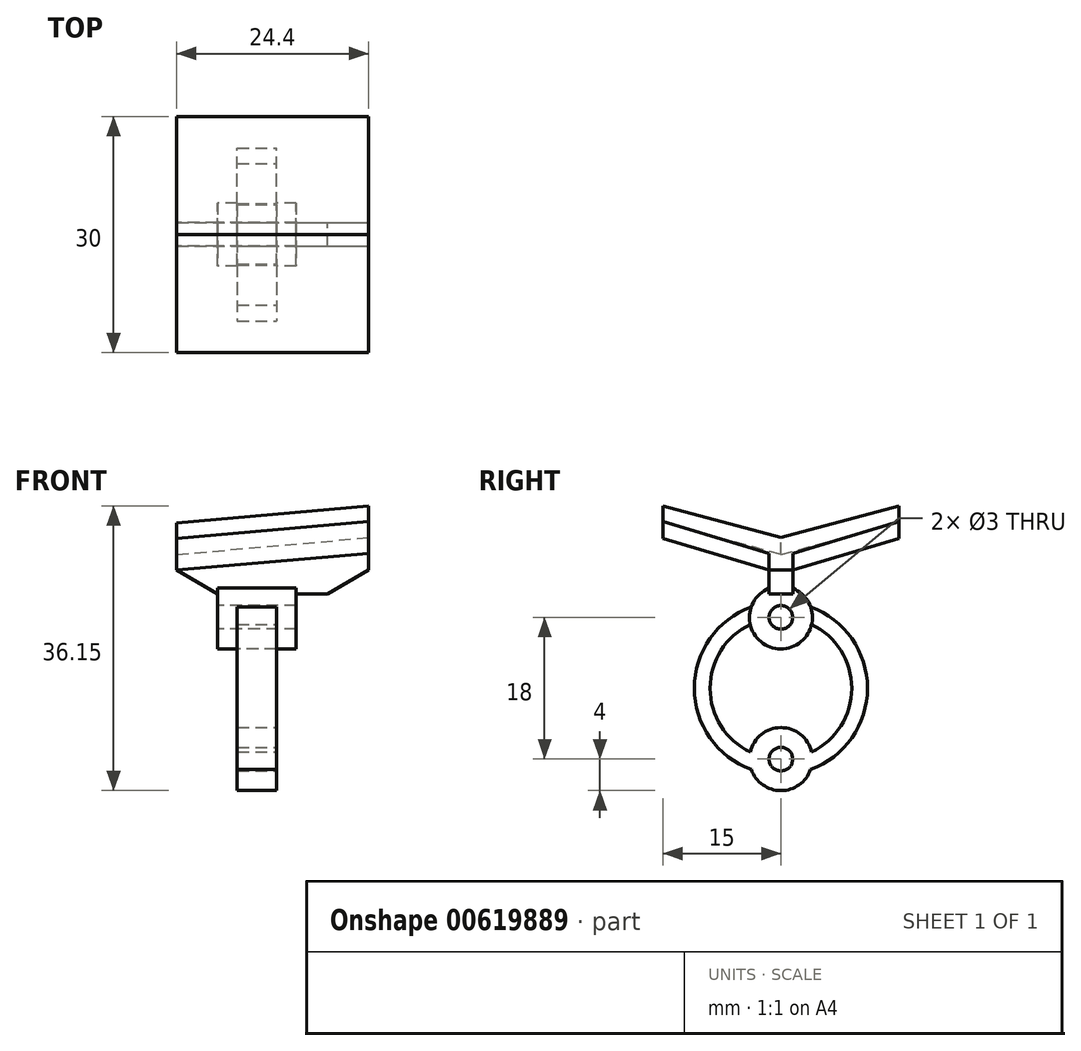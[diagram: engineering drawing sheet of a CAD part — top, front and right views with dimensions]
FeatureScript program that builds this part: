
annotation { "Feature Type Name" : "Feature", "Feature Type Description" : "" }
export const myFeature = defineFeature(function(context is Context, id is Id, definition is map)
    precondition{}
    {
        {
            var Q0;
            Q0=qCreatedBy(makeId("Right.planeOp"),FACE);
            var sketch = newSketch(context, id + "F0", { "sketchPlane" : qUnion([Q0])});
            skCircle(sketch, "E0", {"center": v(0, 0) * mm, "radius": 1.5 * mm});
            skCircle(sketch, "E1", {"center": v(0, 0) * mm, "radius": 4 * mm});
            skSolve(sketch);
        }
        {
            var Q0;
            Q0=makeQuery(id+"F0.imprint","IMPRINT",FACE,{"disambiguationData":[TD([[makeQuery(id+"F0.imprint","IMPRINT",EDGE,{"derivedFrom":sQuery(id+"F0.wireOp",EDGE,"E0")}),-1.0]])]});
            var Q1;
            Q1=qConstructionFilter(qBodyType(qCreatedBy(id+"F0",EDGE),BodyType.WIRE),ConstructionObject.NO);
            extrude(context, id + "F1", {"entities" : qUnion([Q0]), "surfaceEntities" : qUnion([Q1]), "depth" : 10 * mm, "offsetDistance" : 25 * mm});
        }
        {
            var Q0;
            Q0=qCreatedBy(makeId("Front.planeOp"),FACE);
            var sketch = newSketch(context, id + "F2", { "sketchPlane" : qUnion([Q0])});
            skLineSegment(sketch, "E2", {"start": v(0, 3) * mm, "end": v(14, 3) * mm});
            skLineSegment(sketch, "E3", {"start": v(0, 3) * mm, "end": v(-5.2, 6) * mm});
            skLineSegment(sketch, "E4", {"start": v(14, 3) * mm, "end": v(19.2, 6) * mm});
            skLineSegment(sketch, "E5", {"start": v(-5.2, 6) * mm, "end": v(-5.2, 8) * mm});
            skLineSegment(sketch, "E6", {"start": v(-5.2, 8) * mm, "end": v(19.2, 10.13) * mm});
            skLineSegment(sketch, "E7", {"start": v(19.2, 10.13) * mm, "end": v(19.2, 6) * mm});
            skSolve(sketch);
        }
        {
            var Q0;
            Q0=qSketchRegion(id+"F2",true);
            extrude(context, id + "F3", {"entities" : qUnion([Q0]), "operationType" : NewBodyOperationType.ADD, "endBound" : BoundingType.SYMMETRIC, "depth" : 3 * mm, "offsetDistance" : 25 * mm});
        }
        {
            var Q0;
            Q0=makeQuery(id+"F3.opExtrude","SWEPT_FACE",FACE,{"disambiguationData":[OSD([sQuery(id+"F2.wireOp",EDGE,"E5")])]});
            var sketch = newSketch(context, id + "F4", { "sketchPlane" : qUnion([Q0])});
            skLineSegment(sketch, "E8", {"start": v(0, 8) * mm, "end": v(0, 13) * mm, "construction": true});
            skPoint(sketch, "E8.endSnap0", {"position": v(0, 8) * mm});
            skLineSegment(sketch, "E9", {"start": v(0, 8) * mm, "end": v(15, 12.02) * mm});
            skLineSegment(sketch, "E10", {"start": v(0, 8) * mm, "end": v(10.53, 8) * mm, "construction": true});
            skLineSegment(sketch, "E11", {"start": v(15, 12.02) * mm, "end": v(15, 10.02) * mm});
            skLineSegment(sketch, "E12", {"start": v(15, 10.02) * mm, "end": v(1.5, 6) * mm});
            skLineSegment(sketch, "E13", {"start": v(1.5, 6) * mm, "end": v(0, 8) * mm});
            skLineSegment(sketch, "E14.MirrorCS", {"start": v(0, 8) * mm, "end": v(-15, 12.02) * mm});
            skLineSegment(sketch, "E15.MirrorCS", {"start": v(-1.5, 6) * mm, "end": v(0, 8) * mm});
            skLineSegment(sketch, "E16.MirrorCS", {"start": v(-15, 10.02) * mm, "end": v(-1.5, 6) * mm});
            skLineSegment(sketch, "E17.MirrorCS", {"start": v(-15, 12.02) * mm, "end": v(-15, 10.02) * mm});
            skSolve(sketch);
        }
        {
            var Q0;
            Q0=makeQuery(id+"F3.opExtrude","SWEPT_FACE",FACE,{"disambiguationData":[OSD([sQuery(id+"F2.wireOp",EDGE,"E6")])]});
            var sketch = newSketch(context, id + "F5", { "sketchPlane" : qUnion([Q0])});
            skLineSegment(sketch, "E18", {"start": v(-4.48, 0) * mm, "end": v(20, 0) * mm});
            skSolve(sketch);
        }
        {
            var Q0;
            Q0 = qSketchRegion(id + "F4", true);
            var Q1;
            Q1 = qConstructionFilter(qBodyType(qCreatedBy(id + "F5" ,EDGE), BodyType.WIRE), ConstructionObject.NO);
            sweep(context, id + "F6", {"operationType" : NewBodyOperationType.ADD, "profiles" : qUnion([Q0]), "path" : qUnion([Q1])});
        }
        {
            var Q0;
            Q0=makeQuery(id+"F1.opExtrude","CAP_FACE",FACE,{"disambiguationData":[OSD([sQuery(id+"F0.wireOp",EDGE,"E0"),sQuery(id+"F0.wireOp",EDGE,"E1")])],"isStart":true});
            cPlane(context, id + "F7", {"entities" : qUnion([Q0]), "cplaneType" : CPlaneType.OFFSET, "offset" : 7.5 * mm, "oppositeDirection" : true, "width" : 150 * mm, "height" : 150 * mm});
        }
        {
            var Q0;
            Q0=qCreatedBy(id+"F7.planeOp",FACE);
            var sketch = newSketch(context, id + "F8", { "sketchPlane" : qUnion([Q0])});
            skLineSegment(sketch, "E19", {"start": v(0, 0) * mm, "end": v(0, -18) * mm, "construction": true});
            skCircle(sketch, "E20", {"center": v(0, -18) * mm, "radius": 1.5 * mm});
            skArc(sketch, "E21", {"start": v(3.9, -17.11) * mm, "mid": v(0, -14) * mm, "end": v(-3.9, -17.11) * mm});
            skArc(sketch, "E22", {"start": v(3.9, -17.11) * mm, "mid": v(9, -9) * mm, "end": v(3.9, -0.89) * mm});
            skArc(sketch, "E23.0", {"start": v(-3.77, 1.33) * mm, "mid": v(-11, -9) * mm, "end": v(-3.77, -19.33) * mm});
            skArc(sketch, "E24.0", {"start": v(3.77, 1.33) * mm, "mid": v(4, 0.23) * mm, "end": v(3.9, -0.89) * mm});
            skPoint(sketch, "E25.orphan", {"position": v(1.5, 3.7) * mm});
            skPoint(sketch, "E26.orphan", {"position": v(-1.5, 3.7) * mm});
            skArc(sketch, "E27.trimOffspring", {"start": v(-3.9, -0.89) * mm, "mid": v(-4, 0.23) * mm, "end": v(-3.77, 1.33) * mm});
            skArc(sketch, "E28.trimOffspring", {"start": v(3.77, -19.33) * mm, "mid": v(11, -9) * mm, "end": v(3.77, 1.33) * mm});
            skArc(sketch, "E29.trimOffspring", {"start": v(-3.77, -19.33) * mm, "mid": v(0, -22) * mm, "end": v(3.77, -19.33) * mm});
            skArc(sketch, "E30.trimOffspring", {"start": v(-3.9, -0.89) * mm, "mid": v(-9, -9) * mm, "end": v(-3.9, -17.11) * mm});
            skSolve(sketch);
        }
        {
            var Q0;
            Q0 = qSketchRegion(id + "F8", true);
            extrude(context, id + "F9", {"entities" : qUnion([Q0]), "operationType" : NewBodyOperationType.ADD, "depth" : 5 * mm, "offsetDistance" : 25 * mm});
        }
    });
